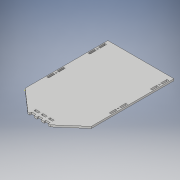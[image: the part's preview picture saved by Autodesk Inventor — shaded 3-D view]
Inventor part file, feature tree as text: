
AUTODESK INVENTOR PART (.ipt)
format: ipt  version: 2018 (Build 220112000, 112)  size: 249,856 bytes
history: native  units: in
note: dims shown in document units (in); Inventor stores cm internally (conversion verified against a paired STEP export)
features: sketch x5, extrude x4
ambient origin geometry x8: Origin, YZ Plane, XZ Plane, XY Plane, X Axis, Y Axis, Z Axis, Center Point
bodies: Body1 (feature_tree)
feature tree (9):
  sketch  "Sketch1"  dims[d18=8.0in d19=10.0in]
  extrude  "Extrusion2"  Depth=10.0in
  extrude  "Extrusion3"  Depth=0.25in
  extrude  "Extrusion4"  Depth=0.1562in
  extrude  "Extrusion5"  Depth=0.75in
  sketch  "Sketch4"  dims[d29=0.75in d30=0.25in]
  sketch  "Sketch5"  dims[d32=0.375in d33=0.1562in]
  sketch  "Sketch6"  dims[d35=0.125in d36=0.75in]
  sketch  "Sketch7"  dims[d39=0.2188in d40=0.0in d57=1.0in d58=0.0in d63=1.0in d64=0.0in d65=0.2188in d67=0.2188in d69=0.2188in d70=0.0in]
